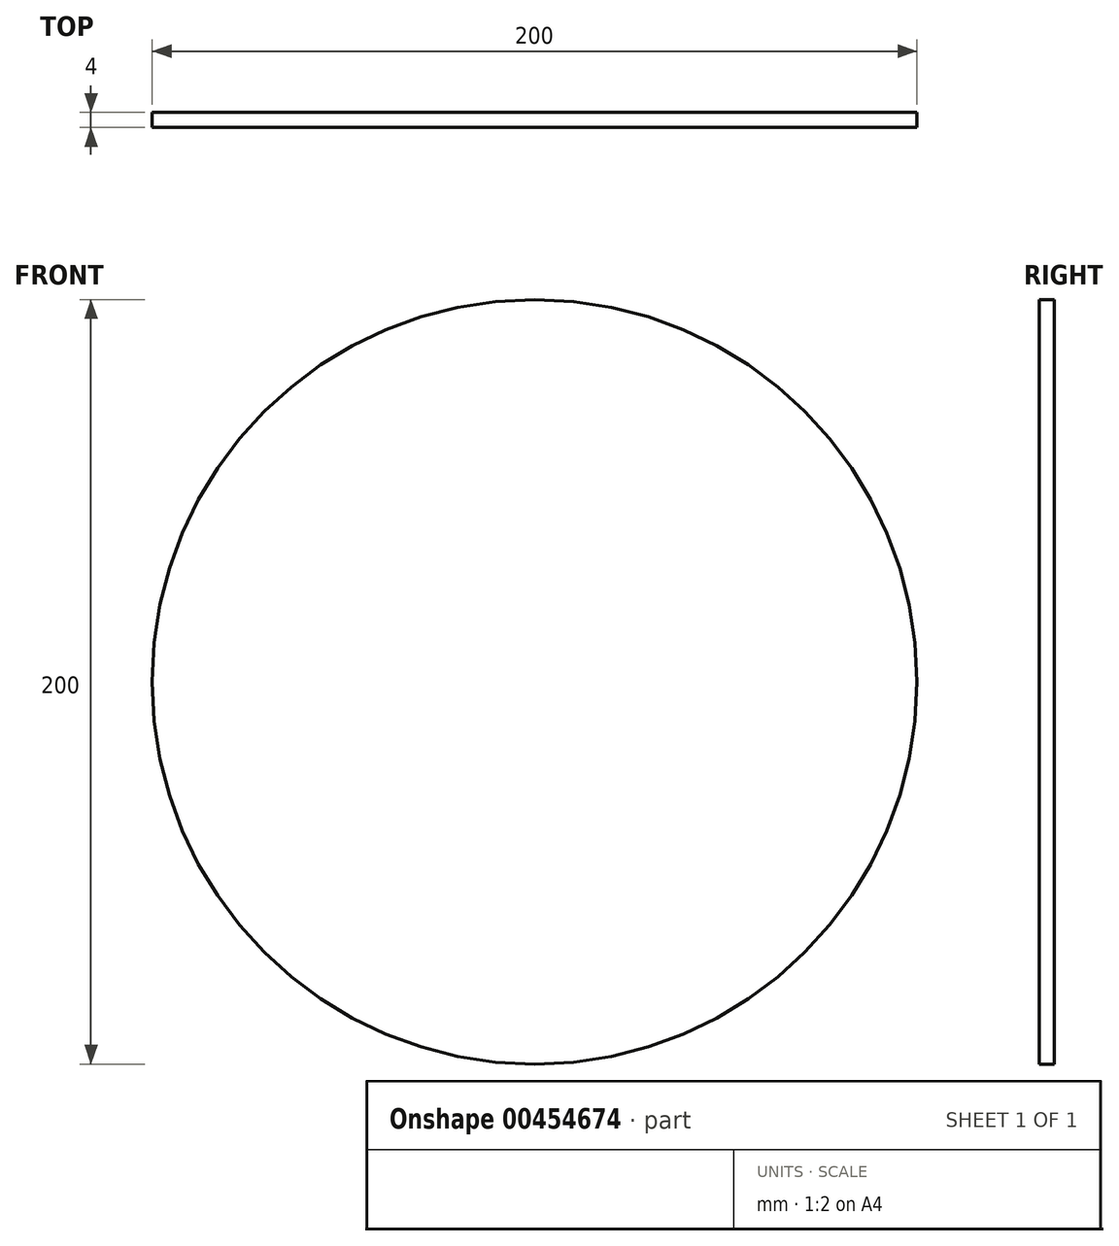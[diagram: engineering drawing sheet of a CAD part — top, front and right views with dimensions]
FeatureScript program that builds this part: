
annotation { "Feature Type Name" : "Feature", "Feature Type Description" : "" }
export const myFeature = defineFeature(function(context is Context, id is Id, definition is map)
    precondition{}
    {
        {
            var Q0;
            Q0=qCreatedBy(makeId("Front.planeOp"),FACE);
            var sketch = newSketch(context, id + "F0", { "sketchPlane" : qUnion([Q0])});
            skCircle(sketch, "E0", {"center": v(0, 0) * mm, "radius": 100 * mm});
            skSolve(sketch);
        }
        {
            var Q0;
            Q0 = qSketchRegion(id + "F0", true);
            extrude(context, id + "F1", {"entities" : qUnion([Q0]), "depth" : 4 * mm, "offsetDistance" : 25 * mm});
        }
    });
